# Revit family: Emergency_Equipment-Tepid-Floor_Mounted_Combination_Shower-S5515
name_source: partatom
category: Plumbing Fixtures
revit_build: Autodesk Revit Architecture 2016 (Build: 20150220_1215(x64)
units: mm (PartAtom-declared; Revit-internal decimal feet)

## family parameters
Always vertical = Yes
Cut with Voids When Loaded = No
OmniClass Number = 23.45.05.14.24
OmniClass Title = Eye Wash Fountains
Part Type = Normal
Room Calculation Point = No
Round Connector Dimension = Use Diameter
Shared = No
Work Plane-Based = No

## types (24) — shared parameters
C Pipe length = 2.5 "
CW Connection = Yes
Description = Floor Mounted Emergency Shower and Eye-Face Wash
Dimension Disclaimer = Dimensions are ±0.50”. Design and specifications are subject to change without notice.
Drain Connection = 1"
HW Connection = Yes
Height = 97.5 "
Manufacturer = Stingray Systems
Product Documentation Link = http://www.tepid.com
Product Name = Barrier-Free Floor Mounted Combination Emergency Shower & Eye/Face Wash
Product Page URL = http://www.tepid.com
Shower Pull Height = 47 "
Supply Connection = 1"
URL = www.tepid.com
Vent Connection = No
Version = 2016-v1.0a
Waste Connection = Yes

## per-type parameters (varying)
| type | AB Bowl | AB Showerhead | Base Finish | Bowl Material | Filter | Length | Pipe Finish | SS Bowl | SS Showerhead | Showerhead Material | Width |
| S5515-GA-NFT-ABAB | Yes | Yes | Metal - Stingray - Epoxy Coated EP | Plastic - Stingray - ABS AB | Yes | 36.7 " | Metal - Stingray - Galvanized GA | No | No | Plastic - Stingray - ABS AB | 16.3 " |
| S5515-GA-NFT-SSAB | No | Yes | Metal - Stingray - Epoxy Coated EP | Metal - Stingray - Stainless Steel SS | Yes | 36.7 " | Metal - Stingray - Galvanized GA | Yes | No | Plastic - Stingray - ABS AB | 14.3 " |
| S5515-GA-NFT-ABSS | Yes | No | Metal - Stingray - Epoxy Coated EP | Plastic - Stingray - ABS AB | Yes | 32.6 " | Metal - Stingray - Galvanized GA | No | Yes | Metal - Stingray - Stainless Steel SS | 16.3 " |
| S5515-GA-NFT-SSSS | No | No | Metal - Stingray - Epoxy Coated EP | Metal - Stingray - Stainless Steel SS | Yes | 32.6 " | Metal - Stingray - Galvanized GA | Yes | Yes | Metal - Stingray - Stainless Steel SS | 14.3 " |
| S5515-EP-NFT-ABAB | Yes | Yes | Metal - Stingray - Epoxy Coated EP | Plastic - Stingray - ABS AB | Yes | 36.7 " | Metal - Stingray - Epoxy Coated EP | No | No | Plastic - Stingray - ABS AB | 16.3 " |
| S5515-EP-NFT-SSAB | No | Yes | Metal - Stingray - Epoxy Coated EP | Metal - Stingray - Stainless Steel SS | Yes | 36.7 " | Metal - Stingray - Epoxy Coated EP | Yes | No | Plastic - Stingray - ABS AB | 14.3 " |
| S5515-EP-NFT-ABSS | Yes | No | Metal - Stingray - Epoxy Coated EP | Plastic - Stingray - ABS AB | Yes | 32.6 " | Metal - Stingray - Epoxy Coated EP | No | Yes | Metal - Stingray - Stainless Steel SS | 16.3 " |
| S5515-EP-NFT-SSSS | No | No | Metal - Stingray - Epoxy Coated EP | Metal - Stingray - Stainless Steel SS | Yes | 32.6 " | Metal - Stingray - Epoxy Coated EP | Yes | Yes | Metal - Stingray - Stainless Steel SS | 14.3 " |
| S5515-SS-NFT-ABAB | Yes | Yes | Metal - Stingray - Stainless Steel SS | Plastic - Stingray - ABS AB | Yes | 36.7 " | Metal - Stingray - Stainless Steel SS | No | No | Plastic - Stingray - ABS AB | 16.3 " |
| S5515-SS-NFT-SSAB | No | Yes | Metal - Stingray - Stainless Steel SS | Metal - Stingray - Stainless Steel SS | Yes | 36.7 " | Metal - Stingray - Stainless Steel SS | Yes | No | Plastic - Stingray - ABS AB | 14.3 " |
| S5515-SS-NFT-ABSS | Yes | No | Metal - Stingray - Stainless Steel SS | Plastic - Stingray - ABS AB | Yes | 32.6 " | Metal - Stingray - Stainless Steel SS | No | Yes | Metal - Stingray - Stainless Steel SS | 16.3 " |
| S5515-SS-NFT-SSSS | No | No | Metal - Stingray - Stainless Steel SS | Metal - Stingray - Stainless Steel SS | Yes | 32.6 " | Metal - Stingray - Stainless Steel SS | Yes | Yes | Metal - Stingray - Stainless Steel SS | 14.3 " |
| S5515-GA-FLT-ABAB | Yes | Yes | Metal - Stingray - Epoxy Coated EP | Plastic - Stingray - ABS AB | No | 36.7 " | Metal - Stingray - Galvanized GA | No | No | Plastic - Stingray - ABS AB | 16.3 " |
| S5515-GA-FLT-SSAB | No | Yes | Metal - Stingray - Epoxy Coated EP | Metal - Stingray - Stainless Steel SS | No | 36.7 " | Metal - Stingray - Galvanized GA | Yes | No | Plastic - Stingray - ABS AB | 14.3 " |
| S5515-GA-FLT-ABSS | Yes | No | Metal - Stingray - Epoxy Coated EP | Plastic - Stingray - ABS AB | No | 32.6 " | Metal - Stingray - Galvanized GA | No | Yes | Metal - Stingray - Stainless Steel SS | 16.3 " |
| S5515-GA-FLT-SSSS | No | No | Metal - Stingray - Epoxy Coated EP | Metal - Stingray - Stainless Steel SS | No | 32.6 " | Metal - Stingray - Galvanized GA | Yes | Yes | Metal - Stingray - Stainless Steel SS | 14.3 " |
| S5515-EP-FLT-ABAB | Yes | Yes | Metal - Stingray - Epoxy Coated EP | Plastic - Stingray - ABS AB | No | 36.7 " | Metal - Stingray - Epoxy Coated EP | No | No | Plastic - Stingray - ABS AB | 16.3 " |
| S5515-EP-FLT-SSAB | No | Yes | Metal - Stingray - Epoxy Coated EP | Metal - Stingray - Stainless Steel SS | No | 36.7 " | Metal - Stingray - Epoxy Coated EP | Yes | No | Plastic - Stingray - ABS AB | 14.3 " |
| S5515-EP-FLT-ABSS | Yes | No | Metal - Stingray - Epoxy Coated EP | Plastic - Stingray - ABS AB | No | 32.6 " | Metal - Stingray - Epoxy Coated EP | No | Yes | Metal - Stingray - Stainless Steel SS | 16.3 " |
| S5515-EP-FLT-SSSS | No | No | Metal - Stingray - Epoxy Coated EP | Metal - Stingray - Stainless Steel SS | No | 32.6 " | Metal - Stingray - Epoxy Coated EP | Yes | Yes | Metal - Stingray - Stainless Steel SS | 14.3 " |
| S5515-SS-FLT-ABAB | Yes | Yes | Metal - Stingray - Stainless Steel SS | Plastic - Stingray - ABS AB | No | 36.7 " | Metal - Stingray - Stainless Steel SS | No | No | Plastic - Stingray - ABS AB | 16.3 " |
| S5515-SS-FLT-SSAB | No | Yes | Metal - Stingray - Stainless Steel SS | Metal - Stingray - Stainless Steel SS | No | 36.7 " | Metal - Stingray - Stainless Steel SS | Yes | No | Plastic - Stingray - ABS AB | 14.3 " |
| S5515-SS-FLT-ABSS | Yes | No | Metal - Stingray - Stainless Steel SS | Plastic - Stingray - ABS AB | No | 32.6 " | Metal - Stingray - Stainless Steel SS | No | Yes | Metal - Stingray - Stainless Steel SS | 16.3 " |
| S5515-SS-FLT-SSSS | No | No | Metal - Stingray - Stainless Steel SS | Metal - Stingray - Stainless Steel SS | No | 32.6 " | Metal - Stingray - Stainless Steel SS | Yes | Yes | Metal - Stingray - Stainless Steel SS | 14.3 " |

note: column(s) folded — value = type name in every type: Model

## geometry (parser evidence)
native form markers: Sweep x13
no freeform markers — native parametric forms only
